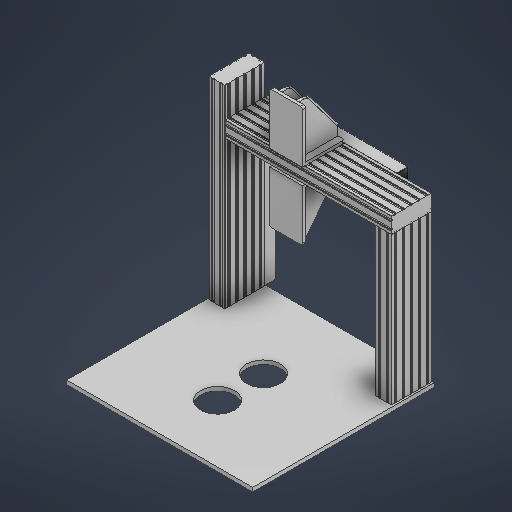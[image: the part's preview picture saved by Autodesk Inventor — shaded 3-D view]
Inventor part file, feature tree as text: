
AUTODESK INVENTOR PART (.ipt)
format: ipt  version: 2025 (Build 290162000, 162)  size: 488,448 bytes
history: native  units: in
note: dims shown in document units (in); Inventor stores cm internally (conversion verified against a paired STEP export)
features: other x14, extrude x1, sketch x1
ambient origin geometry x8: Origin, YZ Plane, XZ Plane, XY Plane, X Axis, Y Axis, Z Axis, Center Point
bodies: Solid1 (feature_tree), Solid2 (feature_tree), Solid3 (feature_tree), Solid4 (feature_tree), Solid5 (feature_tree), Solid6 (feature_tree), Solid7 (feature_tree), Solid8 (feature_tree), Solid9 (feature_tree), Solid10 (feature_tree), Solid11 (feature_tree), Solid12 (feature_tree), Solid13 (feature_tree), Solid14 (feature_tree)
feature tree (16):
  extrude  "Extrusion1"  Depth=11.4173in
  sketch  "Sketch1"  dims[d0=6.6929in d1=11.4173in d2=6.6929in d3=9.0551in d4=0.0in d5=0.0in]
  other  "Base plate"
  other  "Left Tower"
  other  "Right tower"
  other  "Mid Tower"
  other  "Cable Race way Left"
  other  "Cable Raceway Mid"
  other  "Base Top"
  other  "Left Top"
  other  "Right Top"
  other  "Base Bottom"
  other  "Left Bottom"
  other  "Right Bottom"
  other  "Cable Channel Top"
  other  "Cable Cannel Bottom"
